# Revit family: surface no interlocked sockets 480_500V
name_source: partatom
category: Installations électriques
revit_build: Autodesk Revit 2018 (Build: 20170223_1515(x64)
units: mm (PartAtom-declared; Revit-internal decimal feet)

## family parameters
Conserver l'orientation des annotations = Non
Cote de connecteur circulaire = Utiliser le diamètre
Couper avec des vides une fois chargée = Non
Hôte = Face
Partagée = Non
Point de calcul de pièce = Non
Type d'élément = Normal

## types (8) — shared parameters
Elévation par défaut = 1000 mm  [stored 3.28084 ft]
Fabricant = Legrand
International standard socket for flush mounting or surface mounting with accessory allows the connection of power devices = International standard socket for flush mounting or surface mounting with accessory allows the connection of power devices
Maximum use temperature = 40
Minimum installation temperature = -5
Minimum use temperature = -25
Position of earth h = 7
Product family = 0854-P17 TEMPRA PRO
Standard IEC or NFC = IEC
Tension V = 500 V  50/60 Hz black
characteristic color = black
connecting type = screw terminals
interlocking type = x
material of box = plastic
resistance to chocks IK = 9

## per-type parameters (varying)
| type | Description | Diameter cable entry | Modèle | Number of poles | depth mm | halogen free | height mm | horizontal fixing distance mm | intensity A | protection class IP | vertical fixing distance mm | width mm |
| IDS_LG_555162 | IDS_DESCRIPTION_LG_555162 | M20/M25 | LG-555162 | 4 | 133 mm  [stored 0.436352 ft] | Oui | 131 mm  [stored 0.42979 ft] | 70 mm | 16 A | IP44 | 0 mm  [stored 0 ft] | 93 mm |
| IDS_LG_555163 | IDS_DESCRIPTION_LG_555163 | M20/M25 | LG-555163 | 5 | 139 mm | Oui | 131 mm  [stored 0.42979 ft] | 70 mm | 16 A | IP44 | 0 mm  [stored 0 ft] | 93 mm |
| IDS_LG_555262 | IDS_DESCRIPTION_LG_555262 | M25/M32 | LG-555262 | 4 | 155 mm | Oui | 156 mm  [stored 0.511811 ft] | 90 mm | 32 A | IP44 | 0 mm  [stored 0 ft] | 113 mm |
| IDS_LG_555263 | IDS_DESCRIPTION_LG_555263 | M25/M32 | LG-555263 | 5 | 161 mm | Oui | 156 mm  [stored 0.511811 ft] | 90 mm | 32 A | IP44 | 0 mm  [stored 0 ft] | 113 mm |
| IDS_LG_555362 | IDS_DESCRIPTION_LG_555362 | M20/M25 | LG-555362 | 4 | 134 mm  [stored 0.439633 ft] | Non | 138 mm  [stored 0.452756 ft] | 70 mm | 16 A |  | 0 mm  [stored 0 ft] | 93 mm |
| IDS_LG_555462 | IDS_DESCRIPTION_LG_555462 | M25/M32 | LG-555462 | 4 | 156 mm  [stored 0.511811 ft] | Non | 163 mm  [stored 0.534777 ft] | 90 mm | 32 A |  | 0 mm  [stored 0 ft] | 113 mm |
| IDS_LG_555463 | IDS_DESCRIPTION_LG_555463 | M25/M32 | LG-555463 | 5 | 162 mm | Non | 163 mm  [stored 0.534777 ft] | 90 mm | 32 A |  | 0 mm  [stored 0 ft] | 113 mm |
| IDS_LG_555562 | IDS_DESCRIPTION_LG_555562 | M32 | LG-555562 | 4 | 190 mm | Non | 270 mm  [stored 0.885827 ft] | 119 mm | 63 A |  | 156 mm  [stored 0.511811 ft] | 130 mm |

note: [stored X ft] marks values corroborated as IEEE doubles in the binary element streams (Revit-internal decimal feet)
